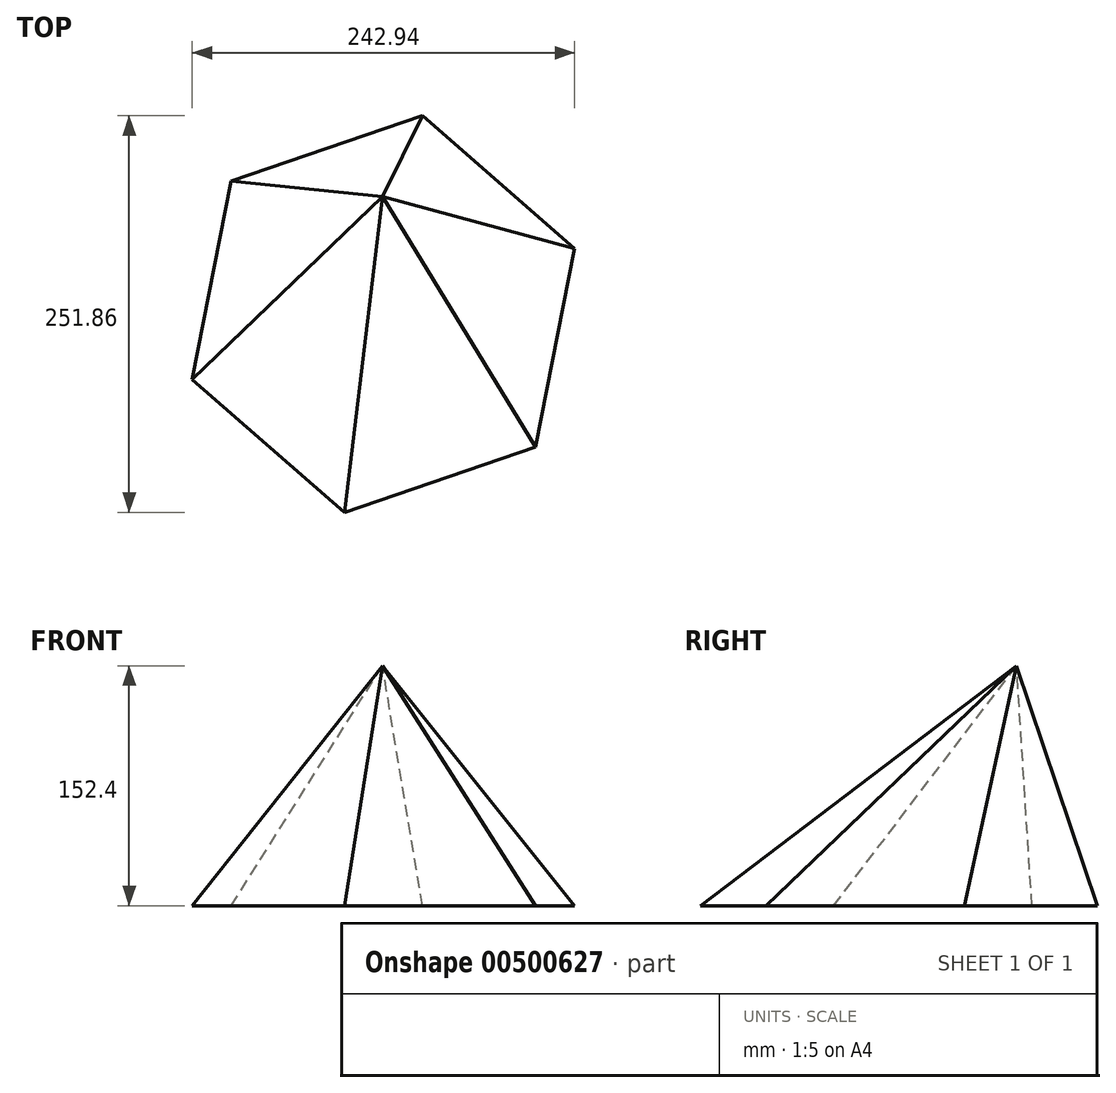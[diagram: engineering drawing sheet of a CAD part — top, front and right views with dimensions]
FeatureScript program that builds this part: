
annotation { "Feature Type Name" : "Feature", "Feature Type Description" : "" }
export const myFeature = defineFeature(function(context is Context, id is Id, definition is map)
    precondition{}
    {
        {
            var Q0;
            Q0=qCreatedBy(makeId("Top.planeOp"),FACE);
            var sketch = newSketch(context, id + "F0", { "sketchPlane" : qUnion([Q0])});
            skCircle(sketch, "E0.cCircle", {"center": v(0, 0) * mm, "radius": 128.36 * mm, "construction": true});
            skLineSegment(sketch, "E0.0", {"start": v(121.47, 41.48) * mm, "end": v(96.66, -84.46) * mm});
            skLineSegment(sketch, "E0.1", {"start": v(96.66, -84.46) * mm, "end": v(-24.81, -125.93) * mm});
            skLineSegment(sketch, "E0.2", {"start": v(-24.81, -125.93) * mm, "end": v(-121.47, -41.48) * mm});
            skLineSegment(sketch, "E0.3", {"start": v(-121.47, -41.48) * mm, "end": v(-96.66, 84.46) * mm});
            skLineSegment(sketch, "E0.4", {"start": v(-96.66, 84.46) * mm, "end": v(24.81, 125.93) * mm});
            skLineSegment(sketch, "E0.5", {"start": v(24.81, 125.93) * mm, "end": v(121.47, 41.48) * mm});
            skSolve(sketch);
        }
        {
            var Q0;
            Q0=makeQuery(id+"F0.imprint","IMPRINT",FACE,{"disambiguationData":[TD([[makeQuery(id+"F0.imprint","IMPRINT",EDGE,{"derivedFrom":sQuery(id+"F0.wireOp",EDGE,"E0.0")}),-1.0]])]});
            cPlane(context, id + "F1", {"entities" : qUnion([Q0]), "cplaneType" : CPlaneType.OFFSET, "offset" : 152.4 * mm, "width" : 152.4 * mm, "height" : 152.4 * mm});
        }
        {
            var Q0;
            Q0=qCreatedBy(id+"F1.planeOp",FACE);
            var sketch = newSketch(context, id + "F2", { "sketchPlane" : qUnion([Q0])});
            skPoint(sketch, "E1", {"position": v(-0.62, 74.75) * mm});
            skSolve(sketch);
        }
        {
            var Q0;
            Q0=makeQuery(id+"F0.imprint","IMPRINT",FACE,{"disambiguationData":[TD([[makeQuery(id+"F0.imprint","IMPRINT",EDGE,{"derivedFrom":sQuery(id+"F0.wireOp",EDGE,"E0.0")}),-1.0]])]});
            var Q1;
            Q1=sQuery(id+"F2.wireOp",VERTEX,"E1");
            loft(context, id + "F3", {"sheetProfilesArray" : [{ "sheetProfileEntities" : qUnion([Q0]) }, { "sheetProfileEntities" : qUnion([Q1]) }]});
        }
    });
